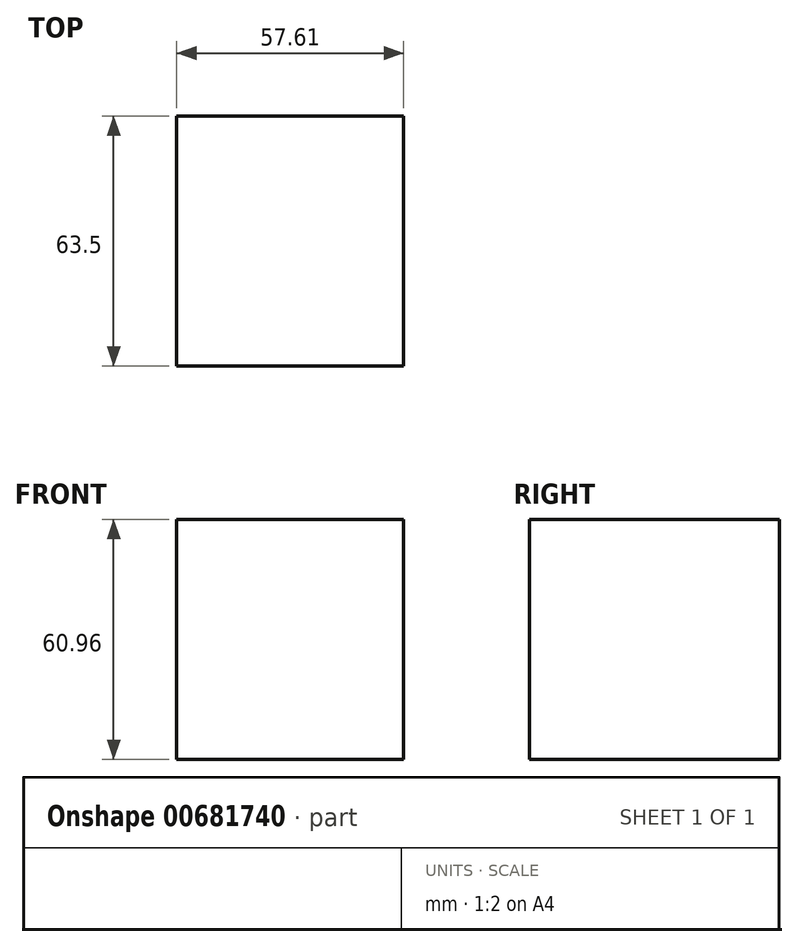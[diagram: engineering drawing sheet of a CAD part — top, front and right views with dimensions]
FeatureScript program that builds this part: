
annotation { "Feature Type Name" : "Feature", "Feature Type Description" : "" }
export const myFeature = defineFeature(function(context is Context, id is Id, definition is map)
    precondition{}
    {
        {
            var Q0;
            Q0=qCreatedBy(makeId("Front.planeOp"),FACE);
            var sketch = newSketch(context, id + "F0", { "sketchPlane" : qUnion([Q0])});
            skLineSegment(sketch, "E0.bottom", {"start": v(-59.51, 60.96) * mm, "end": v(-1.9, 60.96) * mm});
            skLineSegment(sketch, "E0.top", {"start": v(-59.51, 0) * mm, "end": v(-1.9, 0) * mm});
            skLineSegment(sketch, "E0.left", {"start": v(-59.51, 60.96) * mm, "end": v(-59.51, 0) * mm});
            skLineSegment(sketch, "E0.right", {"start": v(-1.9, 60.96) * mm, "end": v(-1.9, 0) * mm});
            skSolve(sketch);
        }
        {
            var Q0;
            Q0=makeQuery(id+"F0.imprint","IMPRINT",FACE,{"disambiguationData":[TD([[makeQuery(id+"F0.imprint","IMPRINT",EDGE,{"derivedFrom":sQuery(id+"F0.wireOp",EDGE,"E0.bottom")}),-1.0]])]});
            extrude(context, id + "F1", {"entities" : qUnion([Q0]), "depth" : 63.5 * mm, "offsetDistance" : 25.4 * mm});
        }
    });
